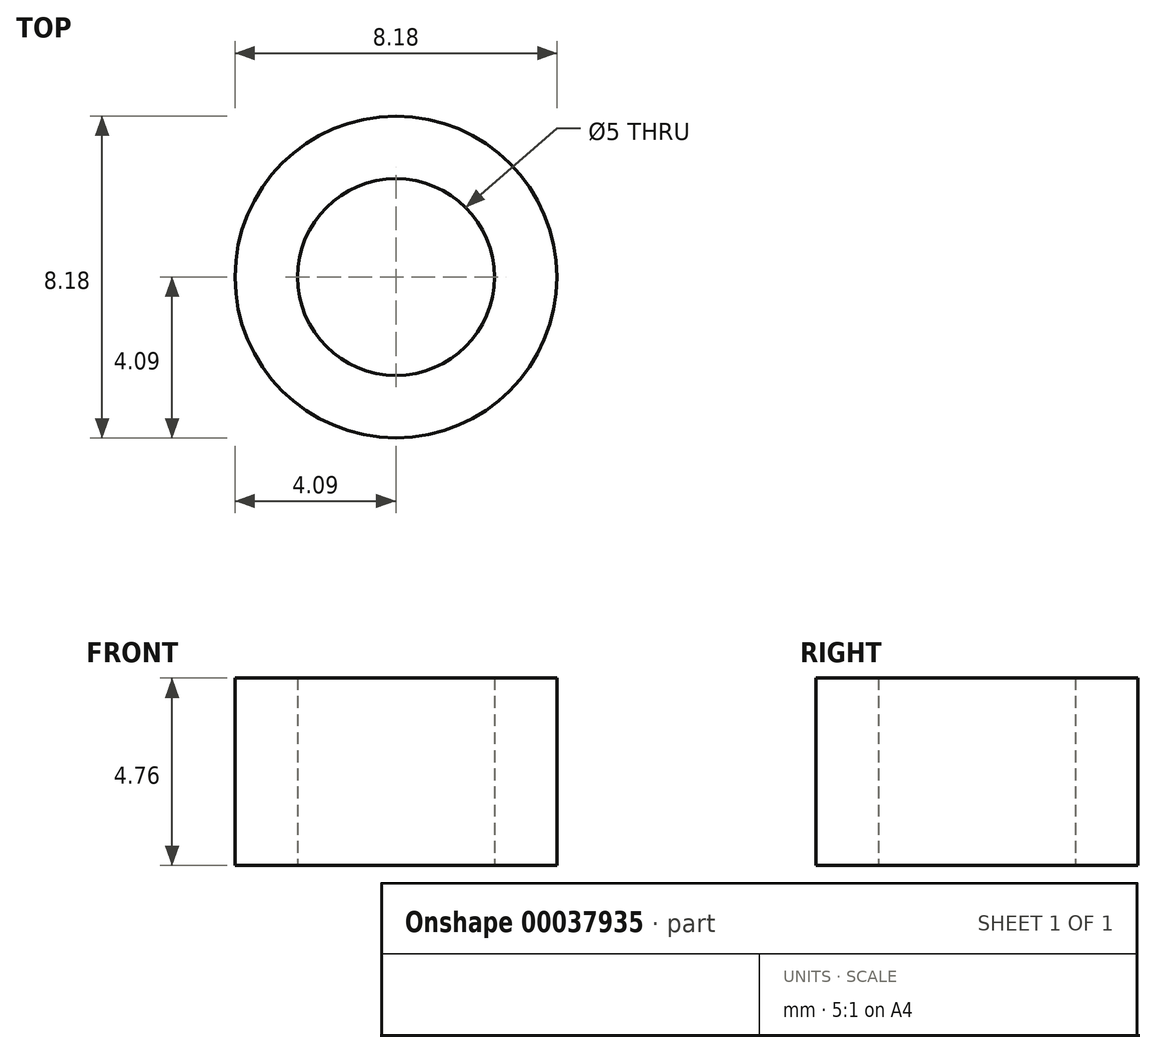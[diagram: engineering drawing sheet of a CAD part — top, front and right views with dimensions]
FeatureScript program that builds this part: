
annotation { "Feature Type Name" : "Feature", "Feature Type Description" : "" }
export const myFeature = defineFeature(function(context is Context, id is Id, definition is map)
    precondition{}
    {
        {
            var Q0;
            Q0=qCreatedBy(makeId("Top.planeOp"),FACE);
            var sketch = newSketch(context, id + "F0", { "sketchPlane" : qUnion([Q0])});
            skCircle(sketch, "E0", {"center": v(0, 0) * mm, "radius": 2.5 * mm});
            skCircle(sketch, "E1", {"center": v(0, 0) * mm, "radius": 4.09 * mm});
            skSolve(sketch);
        }
        {
            var Q0;
            Q0 = qSketchRegion(id + "F0", true);
            extrude(context, id + "F1", {"entities" : qUnion([Q0]), "depth" : 4.76 * mm});
        }
    });
